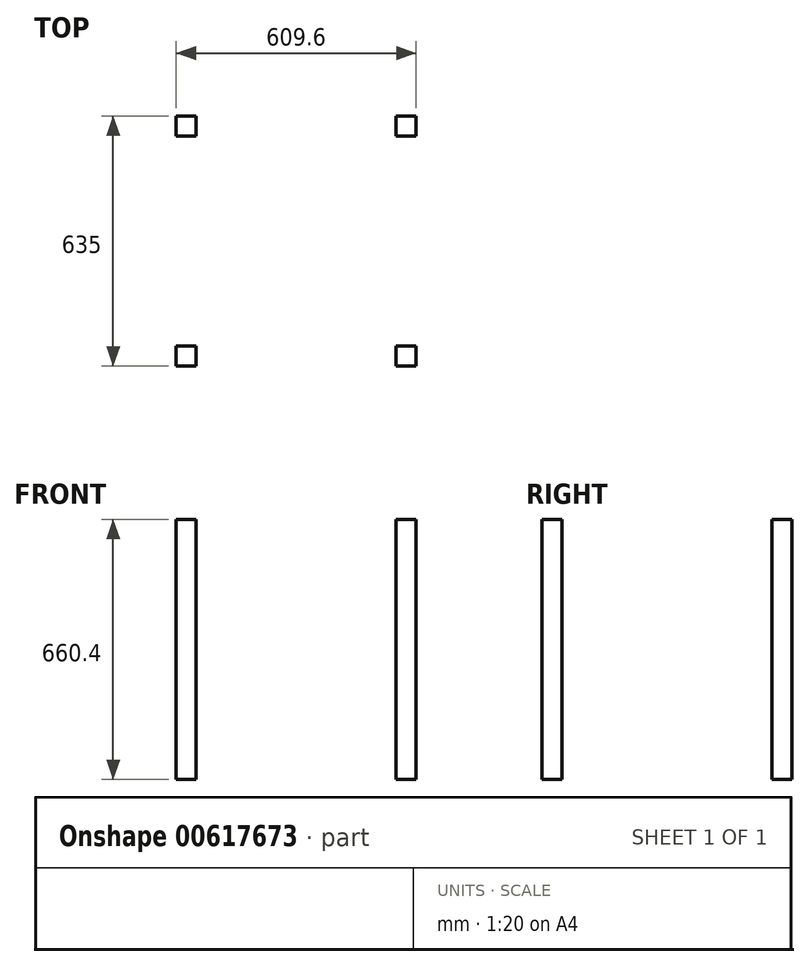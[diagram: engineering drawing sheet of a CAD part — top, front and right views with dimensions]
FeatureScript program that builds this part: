
annotation { "Feature Type Name" : "Feature", "Feature Type Description" : "" }
export const myFeature = defineFeature(function(context is Context, id is Id, definition is map)
    precondition{}
    {
        {
            var Q0;
            Q0=qCreatedBy(makeId("Top.planeOp"),FACE);
            var sketch = newSketch(context, id + "F0", { "sketchPlane" : qUnion([Q0])});
            skLineSegment(sketch, "E0.bottom", {"start": v(-50.8, 380.73) * mm, "end": v(0, 380.73) * mm});
            skLineSegment(sketch, "E0.top", {"start": v(-50.8, 329.93) * mm, "end": v(0, 329.93) * mm});
            skLineSegment(sketch, "E0.left", {"start": v(-50.8, 380.73) * mm, "end": v(-50.8, 329.93) * mm});
            skLineSegment(sketch, "E0.right", {"start": v(0, 380.73) * mm, "end": v(0, 329.93) * mm});
            skLineSegment(sketch, "E1.bottom", {"start": v(558.8, 329.93) * mm, "end": v(508, 329.93) * mm});
            skLineSegment(sketch, "E1.top", {"start": v(558.8, 380.73) * mm, "end": v(508, 380.73) * mm});
            skLineSegment(sketch, "E1.left", {"start": v(558.8, 329.93) * mm, "end": v(558.8, 380.73) * mm});
            skLineSegment(sketch, "E1.right", {"start": v(508, 329.93) * mm, "end": v(508, 380.73) * mm});
            skPoint(sketch, "E1.middle", {"position": v(533.4, 355.33) * mm});
            skPoint(sketch, "E2.startSnap0", {"position": v(-25.4, 380.73) * mm});
            skPoint(sketch, "E2.startSnap1", {"position": v(0, 355.33) * mm});
            skLineSegment(sketch, "E3.bottom", {"start": v(-330.2, 329.93) * mm, "end": v(-50.8, 329.93) * mm});
            skLineSegment(sketch, "E3.top", {"start": v(-50.8, -203.47) * mm, "end": v(-25.4, -203.47) * mm});
            skLineSegment(sketch, "E4.bottom", {"start": v(-50.8, -203.47) * mm, "end": v(0, -203.47) * mm});
            skLineSegment(sketch, "E4.top", {"start": v(-50.8, -254.27) * mm, "end": v(0, -254.27) * mm});
            skLineSegment(sketch, "E4.left", {"start": v(-50.8, -203.47) * mm, "end": v(-50.8, -254.27) * mm});
            skLineSegment(sketch, "E4.right", {"start": v(0, -203.47) * mm, "end": v(0, -254.27) * mm});
            skLineSegment(sketch, "E5", {"start": v(508, -228.87) * mm, "end": v(533.4, -228.87) * mm});
            skLineSegment(sketch, "E6.bottom", {"start": v(558.8, -203.47) * mm, "end": v(508, -203.47) * mm});
            skLineSegment(sketch, "E6.top", {"start": v(558.8, -254.27) * mm, "end": v(508, -254.27) * mm});
            skLineSegment(sketch, "E6.left", {"start": v(558.8, -203.47) * mm, "end": v(558.8, -254.27) * mm});
            skLineSegment(sketch, "E6.right", {"start": v(508, -203.47) * mm, "end": v(508, -254.27) * mm});
            skPoint(sketch, "E6.middle", {"position": v(533.4, -228.87) * mm});
            skPoint(sketch, "E7.start.orphan", {"position": v(-25.4, 355.33) * mm});
            skSolve(sketch);
        }
        {
            var Q0;
            {var subQ1=sQuery(id+"F0.wireOp",EDGE,"E0.bottom");Q0=makeQuery(id+"F0.imprint","IMPRINT",FACE,{"disambiguationData":[TD([[makeQuery(id+"F0.imprint","IMPRINT",EDGE,{"derivedFrom":subQ1}),-1.0]])]});}
            var Q1;
            {var subQ0=sQuery(id+"F0.wireOp",EDGE,"E0.top");Q1=makeQuery(id+"F0.imprint","IMPRINT",FACE,{"disambiguationData":[TD([[makeQuery(id+"F0.imprint","IMPRINT",EDGE,{"derivedFrom":subQ0}),1.0]])]});}
            var Q2;
            {var subQ1=sQuery(id+"F0.wireOp",EDGE,"E4.top");Q2=makeQuery(id+"F0.imprint","IMPRINT",FACE,{"disambiguationData":[TD([[makeQuery(id+"F0.imprint","IMPRINT",EDGE,{"derivedFrom":subQ1}),1.0]])]});}
            var Q3;
            {var subQ0=sQuery(id+"F0.wireOp",EDGE,"yV3hfflG-pyIP-r44K-McZx-IeizdR2PkGFT");Q3=makeQuery(id+"F0.imprint","IMPRINT",FACE,{"disambiguationData":[TD([[makeQuery(id+"F0.imprint","IMPRINT",EDGE,{"derivedFrom":subQ0}),1.0]])]});}
            var Q4;
            {var subQ1=sQuery(id+"F0.wireOp",EDGE,"E6.bottom");Q4=makeQuery(id+"F0.imprint","IMPRINT",FACE,{"disambiguationData":[TD([[makeQuery(id+"F0.imprint","IMPRINT",EDGE,{"derivedFrom":subQ1}),1.0]])]});}
            var Q5;
            {var subQ1=sQuery(id+"F0.wireOp",EDGE,"E1.bottom");Q5=makeQuery(id+"F0.imprint","IMPRINT",FACE,{"disambiguationData":[TD([[makeQuery(id+"F0.imprint","IMPRINT",EDGE,{"derivedFrom":subQ1}),-1.0]])]});}
            extrude(context, id + "F1", {"entities" : qUnion([Q0, Q1, Q2, Q3, Q4, Q5]), "endBound" : BoundingType.SYMMETRIC, "depth" : 660.4 * mm, "offsetDistance" : 25.4 * mm});
        }
    });
